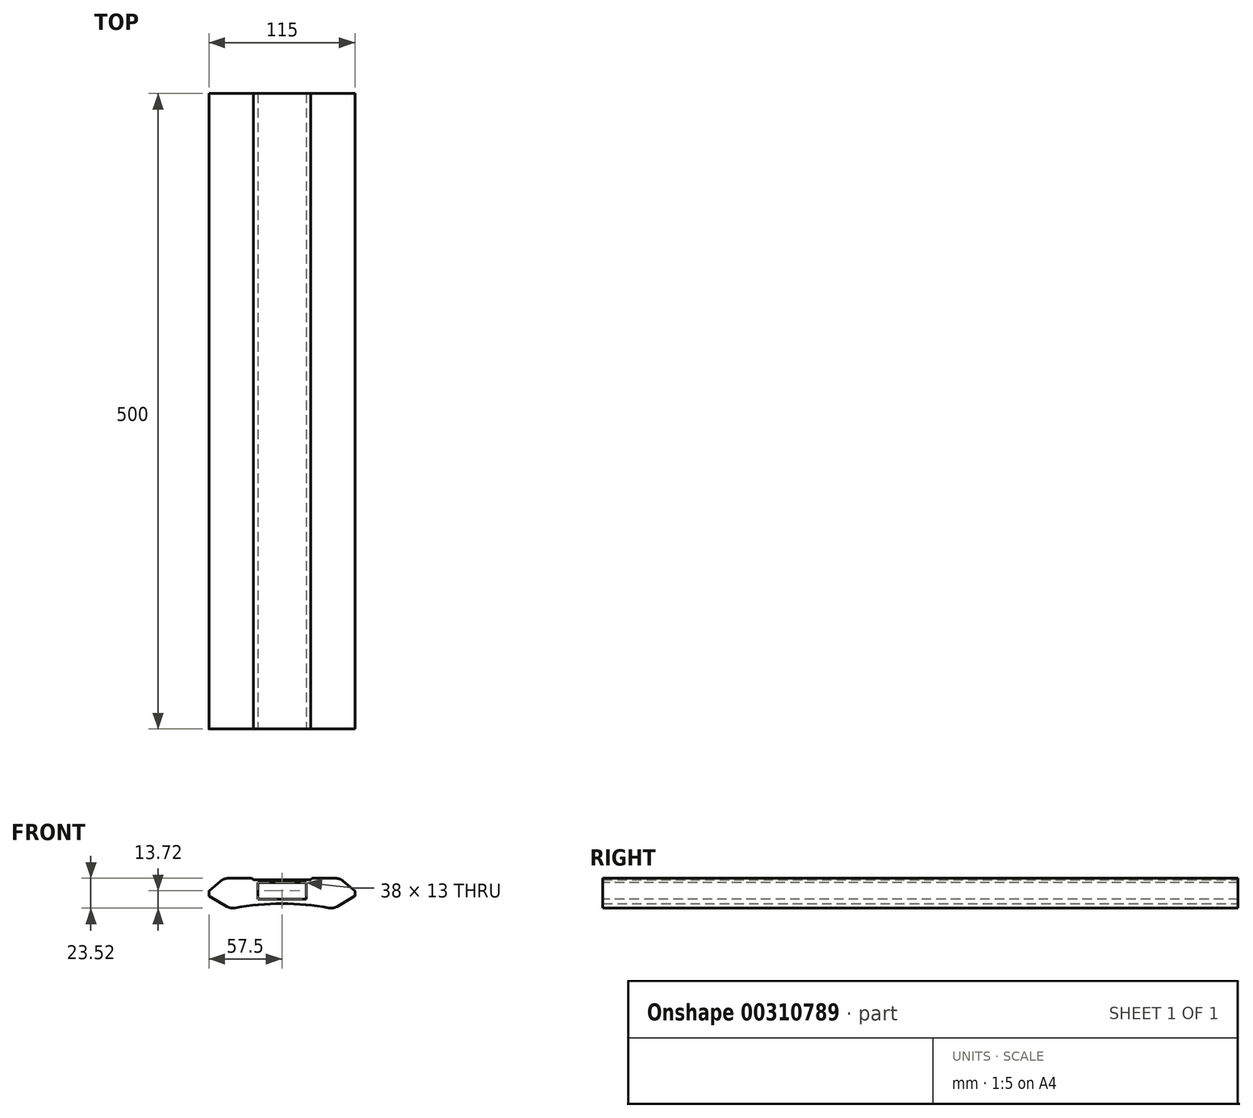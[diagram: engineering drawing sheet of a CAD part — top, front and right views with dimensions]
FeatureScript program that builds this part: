
annotation { "Feature Type Name" : "Feature", "Feature Type Description" : "" }
export const myFeature = defineFeature(function(context is Context, id is Id, definition is map)
    precondition{}
    {
        {
            var Q0;
            Q0=qCreatedBy(makeId("Front.planeOp"),FACE);
            var sketch = newSketch(context, id + "F0", { "sketchPlane" : qUnion([Q0])});
            skLineSegment(sketch, "E0", {"start": v(0, 0) * mm, "end": v(0, 42.64) * mm, "construction": true});
            skLineSegment(sketch, "E1", {"start": v(0, 22.7) * mm, "end": v(22.5, 22.7) * mm});
            skLineSegment(sketch, "E2", {"start": v(22.5, 22.7) * mm, "end": v(22.5, 24) * mm});
            skLineSegment(sketch, "E3", {"start": v(22.5, 24) * mm, "end": v(45.58, 24) * mm});
            skLineSegment(sketch, "E4", {"start": v(45.58, 24) * mm, "end": v(57.5, 14) * mm});
            skLineSegment(sketch, "E5", {"start": v(57.5, 14) * mm, "end": v(57.5, 10) * mm});
            skLineSegment(sketch, "E6", {"start": v(57.5, 10) * mm, "end": v(40.18, 0) * mm});
            skLineSegment(sketch, "E7.MirrorCS", {"start": v(-57.5, 10) * mm, "end": v(-40.18, 0) * mm});
            skLineSegment(sketch, "E8.MirrorCS", {"start": v(-57.5, 14) * mm, "end": v(-57.5, 10) * mm});
            skLineSegment(sketch, "E9.MirrorCS", {"start": v(-22.5, 22.7) * mm, "end": v(-22.5, 24) * mm});
            skLineSegment(sketch, "E10.MirrorCS", {"start": v(0, 22.7) * mm, "end": v(-22.5, 22.7) * mm});
            skLineSegment(sketch, "E11.MirrorCS", {"start": v(-45.58, 24) * mm, "end": v(-57.5, 14) * mm});
            skLineSegment(sketch, "E12.MirrorCS", {"start": v(-22.5, 24) * mm, "end": v(-45.58, 24) * mm});
            skArc(sketch, "E13", {"start": v(40.18, 0) * mm, "mid": v(0, 4.08) * mm, "end": v(-40.18, 0) * mm});
            skSolve(sketch);
        }
        {
            var Q0;
            Q0 = qSketchRegion(id + "F0", true);
            extrude(context, id + "F1", {"entities" : qUnion([Q0]), "endBound" : BoundingType.SYMMETRIC, "depth" : 500 * mm});
        }
        {
            var Q0;
            Q0=makeQuery(id+"F1.opExtrude","CAP_FACE",FACE,{"disambiguationData":[OSD([sQuery(id+"F0.wireOp",EDGE,"E1"),sQuery(id+"F0.wireOp",EDGE,"E2"),sQuery(id+"F0.wireOp",EDGE,"E3"),sQuery(id+"F0.wireOp",EDGE,"E4"),sQuery(id+"F0.wireOp",EDGE,"E5"),sQuery(id+"F0.wireOp",EDGE,"E6"),sQuery(id+"F0.wireOp",EDGE,"E7.MirrorCS"),sQuery(id+"F0.wireOp",EDGE,"E8.MirrorCS"),sQuery(id+"F0.wireOp",EDGE,"E9.MirrorCS"),sQuery(id+"F0.wireOp",EDGE,"E10.MirrorCS"),sQuery(id+"F0.wireOp",EDGE,"E11.MirrorCS"),sQuery(id+"F0.wireOp",EDGE,"E12.MirrorCS"),sQuery(id+"F0.wireOp",EDGE,"E13")])],"isStart":false});
            var sketch = newSketch(context, id + "F2", { "sketchPlane" : qUnion([Q0])});
            skLineSegment(sketch, "E14.bottom", {"start": v(-19, 20.7) * mm, "end": v(19, 20.7) * mm});
            skLineSegment(sketch, "E14.top", {"start": v(-19, 7.7) * mm, "end": v(19, 7.7) * mm});
            skLineSegment(sketch, "E14.left", {"start": v(-19, 20.7) * mm, "end": v(-19, 7.7) * mm});
            skLineSegment(sketch, "E14.right", {"start": v(19, 20.7) * mm, "end": v(19, 7.7) * mm});
            skSolve(sketch);
        }
        {
            var Q0;
            Q0 = qSketchRegion(id + "F2", true);
            extrude(context, id + "F3", {"entities" : qUnion([Q0]), "operationType" : NewBodyOperationType.REMOVE, "endBound" : BoundingType.THROUGH_ALL, "oppositeDirection" : true, "depth" : 500 * mm});
        }
        {
            var Q0;
            Q0=makeQuery(id+"F1.opExtrude","SWEPT_EDGE",EDGE,{"disambiguationData":[OSD([sQuery(id+"F0.wireOp",EDGE,"E9.MirrorCS"),sQuery(id+"F0.wireOp",EDGE,"E12.MirrorCS")])]});
            var Q1;
            Q1=makeQuery(id+"F1.opExtrude","SWEPT_EDGE",EDGE,{"disambiguationData":[OSD([sQuery(id+"F0.wireOp",EDGE,"E2"),sQuery(id+"F0.wireOp",EDGE,"E3")])]});
            fillet(context, id + "F4", {"entities" : qUnion([Q0, Q1]), "radius" : 2 * mm, "tangentPropagation" : true, "allowEdgeOverflow" : false});
        }
        {
            var Q0;
            Q0=makeQuery(id+"F1.opExtrude","SWEPT_EDGE",EDGE,{"disambiguationData":[OSD([sQuery(id+"F0.wireOp",EDGE,"E11.MirrorCS"),sQuery(id+"F0.wireOp",EDGE,"E12.MirrorCS")])]});
            var Q1;
            Q1=makeQuery(id+"F1.opExtrude","SWEPT_EDGE",EDGE,{"disambiguationData":[OSD([sQuery(id+"F0.wireOp",EDGE,"E3"),sQuery(id+"F0.wireOp",EDGE,"E4")])]});
            var Q2;
            Q2=makeQuery(id+"F1.opExtrude","SWEPT_EDGE",EDGE,{"disambiguationData":[OSD([sQuery(id+"F0.wireOp",EDGE,"E7.MirrorCS"),sQuery(id+"F0.wireOp",EDGE,"E13")])]});
            var Q3;
            Q3=makeQuery(id+"F1.opExtrude","SWEPT_EDGE",EDGE,{"disambiguationData":[OSD([sQuery(id+"F0.wireOp",EDGE,"E6"),sQuery(id+"F0.wireOp",EDGE,"E13")])]});
            fillet(context, id + "F5", {"entities" : qUnion([Q0, Q1, Q2, Q3]), "radius" : 9 * mm, "tangentPropagation" : true, "allowEdgeOverflow" : false});
        }
        {
            var Q0;
            {var subQ0=sQuery(id+"F0.wireOp",EDGE,"E3");Q0=makeQuery(id+"F5.opFillet","BLEND_EDGE",EDGE,{"blendedFrom":[makeQuery(id+"F1.opExtrude","SWEPT_EDGE",EDGE,{"disambiguationData":[OSD([subQ0,sQuery(id+"F0.wireOp",EDGE,"E4")])]}),makeQuery(id+"F1.opExtrude","SWEPT_FACE",FACE,{"disambiguationData":[OSD([subQ0])]})],"blendedInto":[makeQuery(id+"F1.opExtrude","SWEPT_FACE",FACE,{"disambiguationData":[OSD([subQ0])]})]});}
            var Q1;
            Q1=makeQuery(id+"F1.opExtrude","SWEPT_EDGE",EDGE,{"disambiguationData":[OSD([sQuery(id+"F0.wireOp",EDGE,"E4"),sQuery(id+"F0.wireOp",EDGE,"E5")])]});
            var Q2;
            Q2=makeQuery(id+"F1.opExtrude","SWEPT_EDGE",EDGE,{"disambiguationData":[OSD([sQuery(id+"F0.wireOp",EDGE,"E5"),sQuery(id+"F0.wireOp",EDGE,"E6")])]});
            var Q3;
            Q3=makeQuery(id+"F1.opExtrude","SWEPT_EDGE",EDGE,{"disambiguationData":[OSD([sQuery(id+"F0.wireOp",EDGE,"E7.MirrorCS"),sQuery(id+"F0.wireOp",EDGE,"E8.MirrorCS")])]});
            var Q4;
            Q4=makeQuery(id+"F1.opExtrude","SWEPT_EDGE",EDGE,{"disambiguationData":[OSD([sQuery(id+"F0.wireOp",EDGE,"E8.MirrorCS"),sQuery(id+"F0.wireOp",EDGE,"E11.MirrorCS")])]});
            fillet(context, id + "F6", {"entities" : qUnion([Q0, Q1, Q2, Q3, Q4]), "radius" : 1 * mm, "tangentPropagation" : true, "allowEdgeOverflow" : false});
        }
    });
